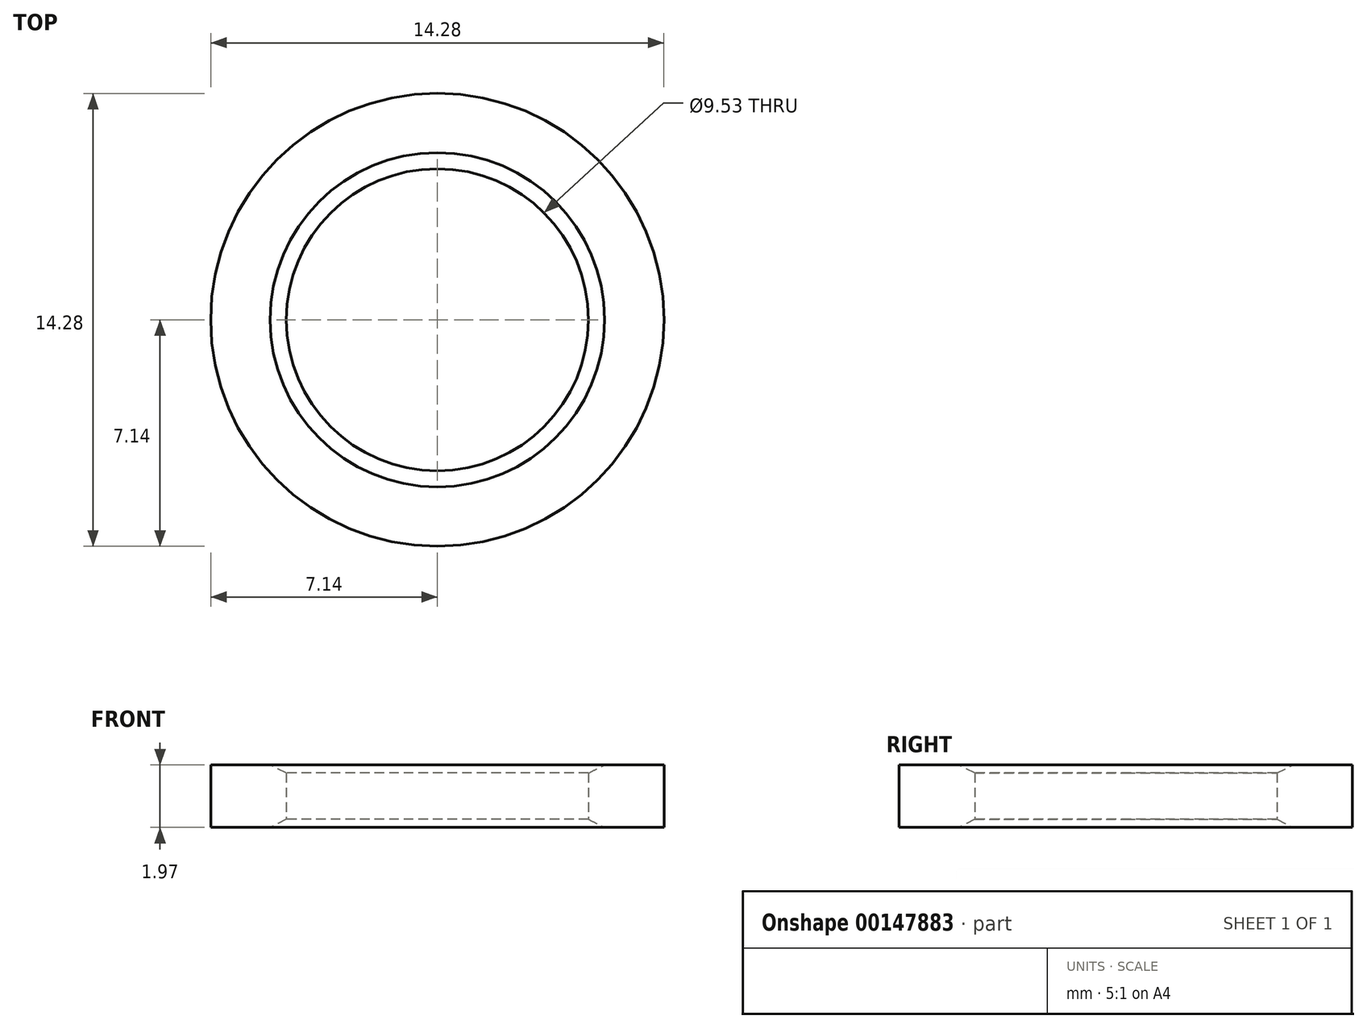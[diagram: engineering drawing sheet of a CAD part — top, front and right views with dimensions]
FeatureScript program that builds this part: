
annotation { "Feature Type Name" : "Feature", "Feature Type Description" : "" }
export const myFeature = defineFeature(function(context is Context, id is Id, definition is map)
    precondition{}
    {
        {
            var Q0;
            Q0=qCreatedBy(makeId("Top.planeOp"),FACE);
            var sketch = newSketch(context, id + "F0", { "sketchPlane" : qUnion([Q0])});
            skCircle(sketch, "E0", {"center": v(0, 0) * mm, "radius": 4.76 * mm});
            skCircle(sketch, "E1", {"center": v(0, 0) * mm, "radius": 7.14 * mm});
            skSolve(sketch);
        }
        {
            var Q0;
            Q0=qSketchRegion(id+"F0",true);
            extrude(context, id + "F1", {"entities" : qUnion([Q0]), "depth" : 1.97 * mm});
        }
        {
            var Q0;
            Q0=makeQuery(id+"F1.opExtrude","CAP_EDGE",EDGE,{"disambiguationData":[OSD([sQuery(id+"F0.wireOp",EDGE,"E0")])],"isStart":false});
            var Q1;
            Q1=makeQuery(id+"F1.opExtrude","CAP_EDGE",EDGE,{"disambiguationData":[OSD([sQuery(id+"F0.wireOp",EDGE,"E0")])],"isStart":true});
            chamfer(context, id + "F2", {"entities" : qUnion([Q0, Q1]), "chamferType" : ChamferType.TWO_OFFSETS, "width1" : 0.25 * mm, "oppositeDirection" : false, "width2" : 0.5 * mm, "tangentPropagation" : true});
        }
    });
